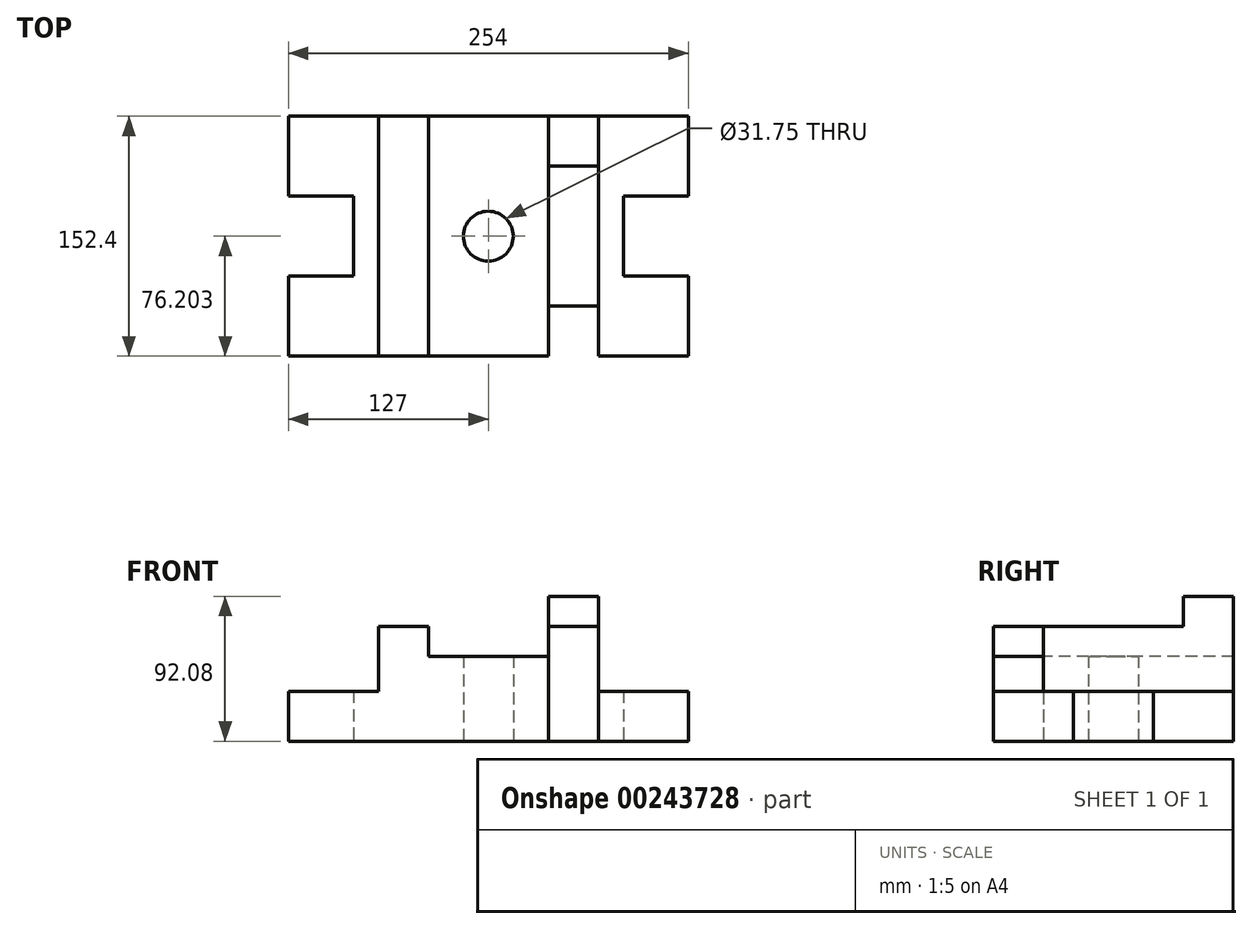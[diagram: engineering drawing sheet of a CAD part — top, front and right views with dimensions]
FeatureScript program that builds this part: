
annotation { "Feature Type Name" : "Feature", "Feature Type Description" : "" }
export const myFeature = defineFeature(function(context is Context, id is Id, definition is map)
    precondition{}
    {
        {
            var Q0;
            Q0=qCreatedBy(makeId("Top.planeOp"),FACE);
            var sketch = newSketch(context, id + "F0", { "sketchPlane" : qUnion([Q0])});
            skLineSegment(sketch, "E0.bottom", {"start": v(127, 61.14) * mm, "end": v(127, 10.34) * mm});
            skLineSegment(sketch, "E0.top", {"start": v(-127, 61.14) * mm, "end": v(-127, 10.34) * mm});
            skLineSegment(sketch, "E0.left", {"start": v(127, 61.14) * mm, "end": v(-127, 61.14) * mm});
            skLineSegment(sketch, "E0.right", {"start": v(127, -91.26) * mm, "end": v(-127, -91.26) * mm});
            skLineSegment(sketch, "E1", {"start": v(-127, -40.46) * mm, "end": v(-85.73, -40.46) * mm});
            skLineSegment(sketch, "E2", {"start": v(-85.73, -40.46) * mm, "end": v(-85.73, 10.34) * mm});
            skLineSegment(sketch, "E3", {"start": v(-85.73, 10.34) * mm, "end": v(-127, 10.34) * mm});
            skLineSegment(sketch, "E4.trimOffspring", {"start": v(-127, -40.46) * mm, "end": v(-127, -91.26) * mm});
            skLineSegment(sketch, "E5", {"start": v(127, 10.34) * mm, "end": v(85.72, 10.34) * mm});
            skLineSegment(sketch, "E6", {"start": v(85.72, 10.34) * mm, "end": v(85.72, -40.46) * mm});
            skLineSegment(sketch, "E7", {"start": v(85.72, -40.46) * mm, "end": v(127, -40.46) * mm});
            skLineSegment(sketch, "E8.trimOffspring", {"start": v(127, -40.46) * mm, "end": v(127, -91.26) * mm});
            skLineSegment(sketch, "E9", {"start": v(-127, 61.14) * mm, "end": v(-69.85, 61.14) * mm});
            skLineSegment(sketch, "E10", {"start": v(-69.85, 61.14) * mm, "end": v(-69.85, -91.26) * mm});
            skLineSegment(sketch, "E11", {"start": v(-127, -91.26) * mm, "end": v(-69.85, -91.26) * mm});
            skLineSegment(sketch, "E12", {"start": v(-127, 61.14) * mm, "end": v(-38.1, 61.14) * mm});
            skLineSegment(sketch, "E13", {"start": v(-38.1, 61.14) * mm, "end": v(-38.1, -91.26) * mm});
            skLineSegment(sketch, "E14", {"start": v(-38.1, 61.14) * mm, "end": v(-38.1, 29.4) * mm});
            skLineSegment(sketch, "E15", {"start": v(-38.1, -91.26) * mm, "end": v(-38.1, -59.5) * mm});
            skLineSegment(sketch, "E16", {"start": v(-38.1, -59.5) * mm, "end": v(-69.85, -59.5) * mm});
            skLineSegment(sketch, "E17", {"start": v(-38.1, 29.4) * mm, "end": v(-69.85, 29.4) * mm});
            skLineSegment(sketch, "E18", {"start": v(-38.1, 61.14) * mm, "end": v(38.1, 61.14) * mm});
            skLineSegment(sketch, "E19", {"start": v(38.1, 61.14) * mm, "end": v(38.1, -91.26) * mm});
            skLineSegment(sketch, "E20", {"start": v(38.1, -91.26) * mm, "end": v(69.85, -91.26) * mm});
            skLineSegment(sketch, "E21", {"start": v(69.85, -91.26) * mm, "end": v(69.85, 61.14) * mm});
            skLineSegment(sketch, "E22", {"start": v(69.85, -59.5) * mm, "end": v(38.1, -59.5) * mm});
            skLineSegment(sketch, "E23", {"start": v(69.85, 29.4) * mm, "end": v(38.1, 29.4) * mm});
            skCircle(sketch, "E24", {"center": v(0, -15.06) * mm, "radius": 15.88 * mm});
            skSolve(sketch);
        }
        {
            var Q0;
            {var subQ0=sQuery(id+"F0.wireOp",EDGE,"E0.bottom");Q0=makeQuery(id+"F0.imprint","IMPRINT",FACE,{"disambiguationData":[TD([[makeQuery(id+"F0.imprint","IMPRINT",EDGE,{"derivedFrom":subQ0}),-1.0]])]});}
            var Q1;
            {var subQ3=sQuery(id+"F0.wireOp",EDGE,"E0.top");Q1=makeQuery(id+"F0.imprint","IMPRINT",FACE,{"disambiguationData":[TD([[makeQuery(id+"F0.imprint","IMPRINT",EDGE,{"derivedFrom":subQ3}),1.0]])]});}
            extrude(context, id + "F1", {"entities" : qUnion([Q0, Q1]), "depth" : 31.75 * mm});
        }
        {
            var Q0;
            Q0=makeQuery(id+"F0.imprint","IMPRINT",FACE,{"disambiguationData":[TD([[makeQuery(id+"F0.imprint","IMPRINT",EDGE,{"derivedFrom":sQuery(id+"F0.wireOp",EDGE,"E13")}),1.0]])]});
            extrude(context, id + "F2", {"entities" : qUnion([Q0]), "depth" : 53.97 * mm});
        }
        {
            var Q0;
            {var subQ0=sQuery(id+"F0.wireOp",EDGE,"E22");Q0=makeQuery(id+"F0.imprint","IMPRINT",FACE,{"disambiguationData":[TD([[makeQuery(id+"F0.imprint","IMPRINT",EDGE,{"derivedFrom":subQ0}),-1.0]])]});}
            var Q1;
            Q1=makeQuery(id+"F0.imprint","IMPRINT",FACE,{"disambiguationData":[TD([[makeQuery(id+"F0.imprint","IMPRINT",EDGE,{"derivedFrom":sQuery(id+"F0.wireOp",EDGE,"E13")}),-1.0]])]});
            extrude(context, id + "F3", {"entities" : qUnion([Q0, Q1]), "operationType" : NewBodyOperationType.ADD, "depth" : 73.02 * mm});
        }
        {
            var Q0;
            {var subQ5=sQuery(id+"F0.wireOp",EDGE,"E23");Q0=makeQuery(id+"F0.imprint","IMPRINT",FACE,{"disambiguationData":[TD([[makeQuery(id+"F0.imprint","IMPRINT",EDGE,{"derivedFrom":subQ5}),-1.0]])]});}
            var Q1;
            {var subQ0=sQuery(id+"F0.wireOp",EDGE,"E20");Q1=makeQuery(id+"F0.imprint","IMPRINT",FACE,{"disambiguationData":[TD([[makeQuery(id+"F0.imprint","IMPRINT",EDGE,{"derivedFrom":subQ0}),1.0]])]});}
            var Q2;
            {var subQ3=sQuery(id+"F0.wireOp",EDGE,"E15");Q2=makeQuery(id+"F0.imprint","IMPRINT",FACE,{"disambiguationData":[TD([[makeQuery(id+"F0.imprint","IMPRINT",EDGE,{"derivedFrom":subQ3}),1.0]])]});}
            var Q3;
            {var subQ4=sQuery(id+"F0.wireOp",EDGE,"E14");Q3=makeQuery(id+"F0.imprint","IMPRINT",FACE,{"disambiguationData":[TD([[makeQuery(id+"F0.imprint","IMPRINT",EDGE,{"derivedFrom":subQ4}),-1.0]])]});}
            extrude(context, id + "F4", {"entities" : qUnion([Q0, Q1, Q2, Q3]), "operationType" : NewBodyOperationType.ADD, "depth" : 92.07 * mm});
        }
    });
